# Revit family: Приточная-вытяжная система с водяным нагревом фреоновым охлаждением
name_source: partatom
category: Оборудование
units: mm (PartAtom-declared; Revit-internal decimal feet)

## family parameters
Всегда вертикально = Да
Классификация = Нет
На основе рабочей плоскости = Нет
Общий = Нет
При загрузке вырезать с полостями = Нет
Размер круглого соединителя = Использовать диаметр
Тип детали = Нормальный
Точка принадлежности помещению = Нет

## types (16) — shared parameters
ADSK_Напряжение = 380 В
ADSK_Свободный напор воздуха = 400.0 Па
Высота рамы = 120 мм
Длина гибкой встаки = 125 мм
Длина клапана FC = 120 мм
zero-valued in all types: Отметка по умолчанию

## per-type parameters (varying)
| type | ADSK_Масса | ADSK_Обозначение | ADSK_Размер_Высота | ADSK_Размер_Ширина | ADSK_Расход воздуха вытяжной | ADSK_Расход теплоносителя | Высота ГВ | Длина камеры смешения | Длина секции вентилятора FA (вытяжка) (по умолчанию) | Коллектор испарителя вход | Коллектор испарителя выход | Мощность двигателя вытяжка | Мощность двигателя приток | Подключение испарителя E | Слив конденсата | Частота вращения двигателя вытяжка | Частота вращения двигателя приток | Ширина ГВ |
| 1А | 424 | ПВ4.1 | 404 мм | 850 мм | 1200.0 кубический метр в час | 0.6 кубический метр в час | 404 мм | 349 мм | 690 мм | 1 х 12мм | 1 х 16мм | 0.6 кВт | 0.6 кВт | 12 мм | 15 мм | 2835 | 2835 | 850 мм |
| 2А | 496 | ПВ4.2 | 505 мм | 980 мм | 2550.0 кубический метр в час | 1.2 кубический метр в час | 505 мм | 349 мм | 690 мм | 1 х 15мм | 1 х 22мм | 0.8 кВт | 1.1 кВт | 15 мм | 15 мм | 2805 | 2830 | 980 мм |
| 16B | 3196 | ПВ4.16 | 2580 мм | 2580 мм | 33000.0 кубический метр в час | 15.6 кубический метр в час | 2580 мм | 1346 мм | 1990 мм | 4 х 28мм | 4 х 35мм | 15.0 кВт | 18.5 кВт | 28 мм | 25 мм | 1460 | 1465 | 2580 мм |
| 3A | 600 | ПВ4.3 | 695 мм | 1080 мм | 3500.0 кубический метр в час | 1.7 кубический метр в час | 695 мм | 383 мм | 740 мм | 1 х 16мм | 1 х 22мм | 1.1 кВт | 1.5 кВт | 16 мм | 15 мм | 2830 | 2880 | 1080 мм |
| 4A | 698 | ПВ4.4 | 695 мм | 1360 мм | 4500.0 кубический метр в час | 2.1 кубический метр в час | 695 мм | 440 мм | 820 мм | 1 х 16мм | 1 х 22мм | 1.5 кВт | 2.2 кВт | 16 мм | 15 мм | 2880 | 2880 | 1360 мм |
| 5A | 758 | ПВ4.5 | 803 мм | 1360 мм | 5500.0 кубический метр в час | 2.6 кубический метр в час | 803 мм | 437 мм | 820 мм | 1 х 16мм | 1 х 22мм | 2.2 кВт | 3.0 кВт | 16 мм | 15 мм | 2880 | 2905 | 1360 мм |
| 6A | 888 | ПВ4.6 | 803 мм | 1580 мм | 6500.0 кубический метр в час | 3.1 кубический метр в час | 803 мм | 437 мм | 850 мм | 1 х 28мм | 1 х 35мм | 3.0 кВт | 2.2 кВт | 28 мм | 15 мм | 2905 | 1455 | 1580 мм |
| 7A | 978 | ПВ4.7 | 990 мм | 1580 мм | 7500.0 кубический метр в час | 3.5 кубический метр в час | 990 мм | 531 мм | 900 мм | 1 х 22мм | 1 х 28мм | 4.0 кВт | 4.0 кВт | 22 мм | 15 мм | 2945 | 2945 | 1580 мм |
| 8A | 1151 | ПВ4.8 | 990 мм | 1950 мм | 85000.0 кубический метр в час | 4.0 кубический метр в час | 990 мм | 531 мм | 1250 мм | 1 х 22мм | 1 х 28мм | 4.0 кВт | 3.0 кВт | 22 мм | 15 мм | 2945 | 1455 | 1950 мм |
| 9A | 1323 | ПВ4.9 | 1095 мм | 2160 мм | 10000.0 кубический метр в час | 4.7 кубический метр в час | 1095 мм | 583 мм | 1350 мм | 1 х 28мм | 1 х 35мм | 3.0 кВт | 3.0 кВт | 28 мм | 15 мм | 1455 | 1455 | 2160 мм |
| 10B | 1663 | ПВ4.10 | 1360 мм | 2040 мм | 13000.0 кубический метр в час | 6.1 кубический метр в час | 1360 мм | 736 мм | 1460 мм | 2 х 28мм | 2 х 35мм | 4.0 кВт | 5.5 кВт | 28 мм | 25 мм | 1460 | 1465 | 2040 мм |
| 12B | 1936 | ПВ4.12 | 1680 мм | 2040 мм | 18000.0 кубический метр в час | 8.5 кубический метр в час | 1680 мм | 896 мм | 1635 мм | 2 х 28мм | 2 х 35мм | 7.5 кВт | 11.0 кВт | 28 мм | 25 мм | 1465 | 1470 | 2040 мм |
| 11B | 1962 | ПВ4.11 | 1360 мм | 2580 мм | 16000.0 кубический метр в час | 7.5 кубический метр в час | 1360 мм | 736 мм | 1635 мм | 2 х 28мм | 2 х 35мм | 5.5 кВт | 7.5 кВт | 28 мм | 25 мм | 1465 | 1465 | 2580 мм |
| 13B | 2224 | ПВ4.13 | 2040 мм | 2040 мм | 20000.0 кубический метр в час | 9.4 кубический метр в час | 2040 мм | 1076 мм | 1635 мм | 1 х 28мм | 1 х 35мм | 7.5 кВт | 11.0 кВт | 28 мм | 25 мм | 1465 | 1470 | 2040 мм |
| 14B | 2350 | ПВ4.14 | 1680 мм | 2580 мм | 23000.0 кубический метр в час | 10.8 кубический метр в час | 1680 мм | 896 мм | 1945 мм | 2 х 28мм | 2 х 35мм | 11.0 кВт | 11.0 кВт | 28 мм | 25 мм | 1470 | 1470 | 2580 мм |
| 15B | 2616 | ПВ4.15 | 2040 мм | 2580 мм | 25000.0 кубический метр в час | 11.8 кубический метр в час | 2040 мм | 1076 мм | 1945 мм | 3 х 28мм | 3 х 35мм | 11.0 кВт | 15.0 кВт | 28 мм | 25 мм | 1470 | 1460 | 2580 мм |
